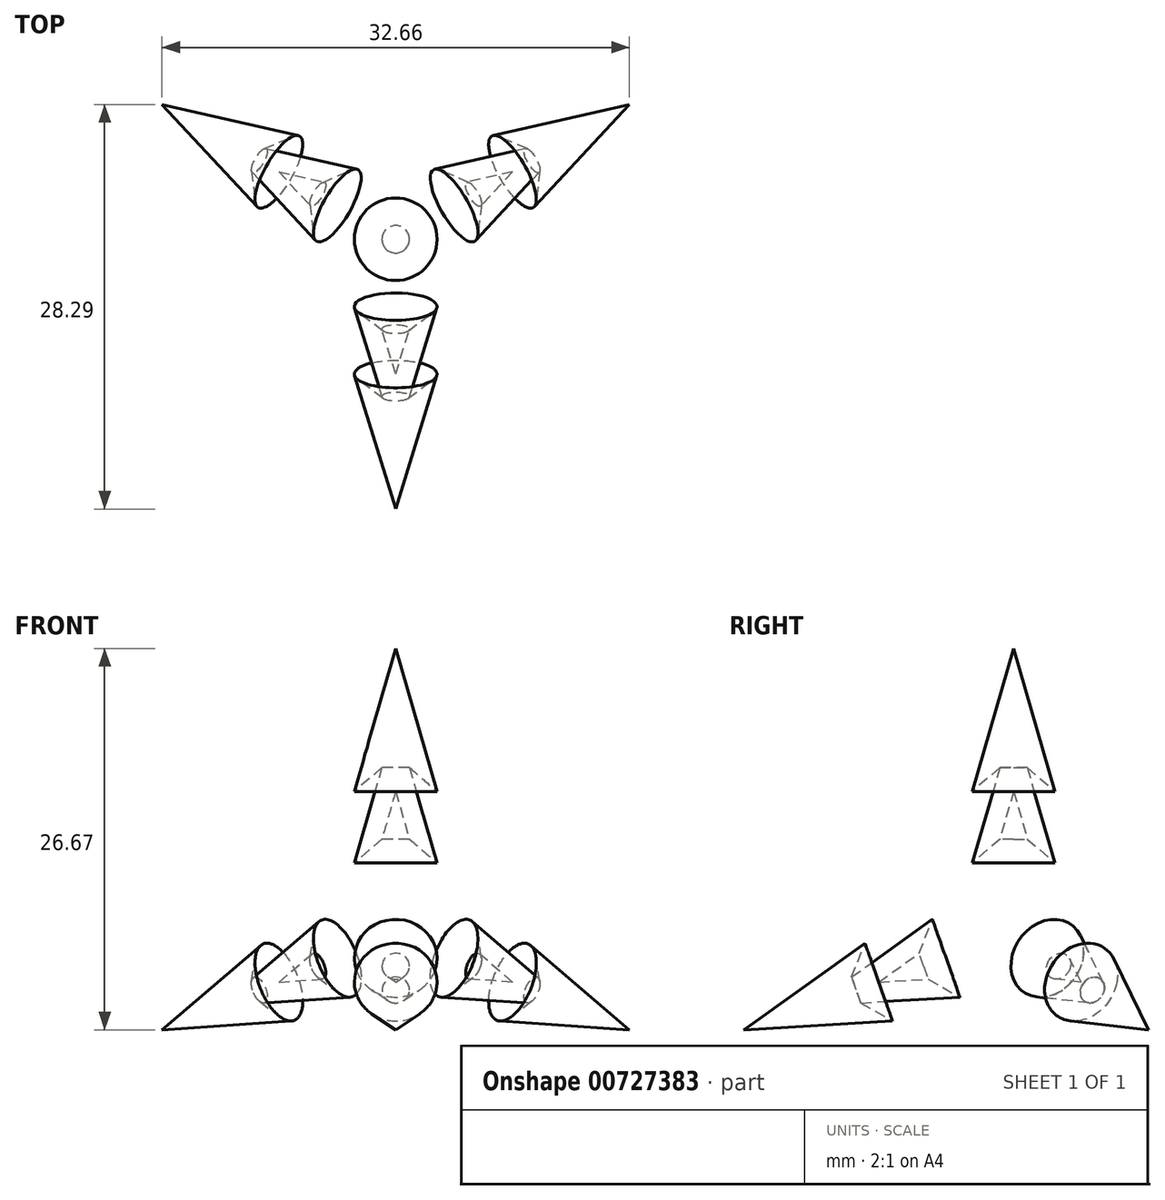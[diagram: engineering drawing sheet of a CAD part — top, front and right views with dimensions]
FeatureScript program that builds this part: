
annotation { "Feature Type Name" : "Feature", "Feature Type Description" : "" }
export const myFeature = defineFeature(function(context is Context, id is Id, definition is map)
    precondition{}
    {
        {
            var Q0;
            Q0=qCreatedBy(makeId("Front.planeOp"),FACE);
            var sketch = newSketch(context, id + "F0", { "sketchPlane" : qUnion([Q0])});
            skCircle(sketch, "E0", {"center": v(0, 0) * mm, "radius": 25 * mm});
            skCircle(sketch, "E1.cCircle", {"center": v(0, 0) * mm, "radius": 25 * mm, "construction": true});
            skLineSegment(sketch, "E2.0", {"start": v(0, 25) * mm, "end": v(21.65, -12.5) * mm});
            skLineSegment(sketch, "E2.1", {"start": v(21.65, -12.5) * mm, "end": v(-21.65, -12.5) * mm});
            skLineSegment(sketch, "E2.2", {"start": v(-21.65, -12.5) * mm, "end": v(0, 25) * mm, "construction": true});
            skLineSegment(sketch, "E3", {"start": v(0, 0) * mm, "end": v(0, 25) * mm});
            skLineSegment(sketch, "E4", {"start": v(0, 0) * mm, "end": v(-14.43, 0) * mm});
            skLineSegment(sketch, "E5", {"start": v(0, 25) * mm, "end": v(0, 20) * mm});
            skLineSegment(sketch, "E6", {"start": v(0, 15) * mm, "end": v(-2.89, 15) * mm, "construction": true});
            skLineSegment(sketch, "E7", {"start": v(-2.89, 15) * mm, "end": v(-2.89, 15) * mm});
            skLineSegment(sketch, "E8", {"start": v(-2.89, 15) * mm, "end": v(0, 25) * mm});
            skLineSegment(sketch, "E9", {"start": v(0, 10) * mm, "end": v(0, 5) * mm});
            skLineSegment(sketch, "E10", {"start": v(0, 0) * mm, "end": v(-2.89, 0) * mm});
            skLineSegment(sketch, "E11", {"start": v(-2.89, 0) * mm, "end": v(0, 10) * mm});
            skLineSegment(sketch, "E12", {"start": v(0, 20) * mm, "end": v(0, 15) * mm});
            skLineSegment(sketch, "E13", {"start": v(0, 10) * mm, "end": v(-2.89, 10) * mm, "construction": true});
            skLineSegment(sketch, "E14", {"start": v(-2.89, 10) * mm, "end": v(0, 20) * mm});
            skPoint(sketch, "E15", {"position": v(0, 5) * mm});
            skLineSegment(sketch, "E16", {"start": v(0, 15) * mm, "end": v(0, 10) * mm});
            skLineSegment(sketch, "E17", {"start": v(0, 5) * mm, "end": v(-2.89, 5) * mm, "construction": true});
            skLineSegment(sketch, "E18", {"start": v(-2.89, 5) * mm, "end": v(0, 15) * mm});
            skLineSegment(sketch, "E19", {"start": v(0, 5) * mm, "end": v(0, 0) * mm});
            skLineSegment(sketch, "E20", {"start": v(0, 17.5) * mm, "end": v(-2.89, 15) * mm});
            skLineSegment(sketch, "E21", {"start": v(0, 12.5) * mm, "end": v(-2.89, 10) * mm});
            skLineSegment(sketch, "E22", {"start": v(0, 7.5) * mm, "end": v(-2.89, 5) * mm});
            skSolve(sketch);
        }
        {
            var Q0;
            Q0=qCreatedBy(makeId("Right.planeOp"),FACE);
            var sketch = newSketch(context, id + "F1", { "sketchPlane" : qUnion([Q0])});
            skCircle(sketch, "E23", {"center": v(0, 0) * mm, "radius": 25 * mm});
            skLineSegment(sketch, "E24", {"start": v(0, 0) * mm, "end": v(0, 25) * mm});
            skCircle(sketch, "E25.cCircle", {"center": v(0, 0) * mm, "radius": 25 * mm, "construction": true});
            skLineSegment(sketch, "E25.0", {"start": v(0, 25) * mm, "end": v(21.65, -12.5) * mm});
            skLineSegment(sketch, "E25.1", {"start": v(21.65, -12.5) * mm, "end": v(-21.65, -12.5) * mm});
            skLineSegment(sketch, "E25.2", {"start": v(-21.65, -12.5) * mm, "end": v(0, 25) * mm});
            skLineSegment(sketch, "E26", {"start": v(0, 0) * mm, "end": v(0, -25) * mm});
            skSolve(sketch);
        }
        {
            var Q0;
            {var subQ0=sQuery(id+"F0.wireOp",EDGE,"E5");Q0=makeQuery(id+"F0.imprint","IMPRINT",FACE,{"disambiguationData":[TD([[makeQuery(id+"F0.imprint","IMPRINT",EDGE,{"derivedFrom":subQ0}),-1.0]])]});}
            var Q1;
            {var subQ0=sQuery(id+"F0.wireOp",EDGE,"E12");var subQ3=sQuery(id+"F0.wireOp",EDGE,"E20");var subQ5=makeQuery(id+"F0.imprint","INTERSECT",VERTEX,{"derivedFrom":[subQ0,subQ3]});Q1=makeQuery(id+"F0.imprint","IMPRINT",FACE,{"disambiguationData":[TD([[makeQuery(id+"F0.imprint","IMPRINT",EDGE,{"disambiguationData":[TD([[subQ5,-1.0]])],"derivedFrom":subQ3}),-1.0]])]});}
            var Q2;
            {var subQ3=sQuery(id+"F0.wireOp",EDGE,"E14");var subQ5=sQuery(id+"F0.wireOp",EDGE,"E21");var subQ6=makeQuery(id+"F0.imprint","INTERSECT",VERTEX,{"derivedFrom":[subQ3,subQ5]});Q2=makeQuery(id+"F0.imprint","IMPRINT",FACE,{"disambiguationData":[TD([[makeQuery(id+"F0.imprint","IMPRINT",EDGE,{"disambiguationData":[TD([[subQ6,-1.0]])],"derivedFrom":subQ3}),-1.0]])]});}
            var Q3;
            {var subQ0=sQuery(id+"F0.wireOp",EDGE,"E16");var subQ3=sQuery(id+"F0.wireOp",EDGE,"E21");var subQ5=makeQuery(id+"F0.imprint","INTERSECT",VERTEX,{"derivedFrom":[subQ0,subQ3]});Q3=makeQuery(id+"F0.imprint","IMPRINT",FACE,{"disambiguationData":[TD([[makeQuery(id+"F0.imprint","IMPRINT",EDGE,{"disambiguationData":[TD([[subQ5,-1.0]])],"derivedFrom":subQ3}),-1.0]])]});}
            var Q4;
            {var subQ3=sQuery(id+"F0.wireOp",EDGE,"E18");var subQ5=sQuery(id+"F0.wireOp",EDGE,"E22");var subQ6=makeQuery(id+"F0.imprint","INTERSECT",VERTEX,{"derivedFrom":[subQ3,subQ5]});Q4=makeQuery(id+"F0.imprint","IMPRINT",FACE,{"disambiguationData":[TD([[makeQuery(id+"F0.imprint","IMPRINT",EDGE,{"disambiguationData":[TD([[subQ6,-1.0]])],"derivedFrom":subQ3}),-1.0]])]});}
            var Q5;
            {var subQ5=sQuery(id+"F0.wireOp",EDGE,"E10");Q5=makeQuery(id+"F0.imprint","IMPRINT",FACE,{"disambiguationData":[TD([[makeQuery(id+"F0.imprint","IMPRINT",EDGE,{"derivedFrom":subQ5}),-1.0]])]});}
            var Q6;
            Q6=sQuery(id+"F0.wireOp",EDGE,"E5");
            revolve(context, id + "F2", {"surfaceOperationType" : NewSurfaceOperationType.NEW, "entities" : qUnion([Q0, Q1, Q2, Q3, Q4, Q5]), "axis" : qUnion([Q6]), "revolveType" : RevolveType.FULL});
        }
        {
            var Q0;
            Q0=qCreatedBy(makeId("Top.planeOp"),FACE);
            var sketch = newSketch(context, id + "F3", { "sketchPlane" : qUnion([Q0])});
            skLineSegment(sketch, "E27", {"start": v(-21.46, 0) * mm, "end": v(21.46, 0) * mm});
            skLineSegment(sketch, "E28", {"start": v(0, 21.76) * mm, "end": v(0, -21.46) * mm});
            skSolve(sketch);
        }
        {
            var Q0;
            Q0=makeQuery(id+"F2.opRevolve","SWEPT_BODY",BODY,{"disambiguationData":[OSD([sQuery(id+"F0.wireOp",EDGE,"E5"),sQuery(id+"F0.wireOp",EDGE,"E8"),sQuery(id+"F0.wireOp",EDGE,"E11"),sQuery(id+"F0.wireOp",EDGE,"E14"),sQuery(id+"F0.wireOp",EDGE,"E18"),sQuery(id+"F0.wireOp",EDGE,"E12"),sQuery(id+"F0.wireOp",EDGE,"E16"),sQuery(id+"F0.wireOp",EDGE,"E20"),sQuery(id+"F0.wireOp",EDGE,"E21"),sQuery(id+"F0.wireOp",EDGE,"E22")])]});
            var Q1;
            Q1=makeQuery(id+"F2.opRevolve","SWEPT_BODY",BODY,{"disambiguationData":[OSD([sQuery(id+"F0.wireOp",EDGE,"E10"),sQuery(id+"F0.wireOp",EDGE,"E11"),sQuery(id+"F0.wireOp",EDGE,"E9"),sQuery(id+"F0.wireOp",EDGE,"E19"),sQuery(id+"F0.wireOp",EDGE,"E22")])]});
            var Q2;
            Q2=sQuery(id+"F3.wireOp",EDGE,"E27");
            transform(context, id + "F4", {"entities" : qUnion([Q0, Q1]), "transformType" : TransformType.ROTATION, "transformAxis" : qUnion([Q2]), "angle" : 109.47 * degree, "makeCopy" : true});
        }
        {
            var Q0;
            Q0=makeQuery(id+"F4.opPattern","COPY",BODY,{"derivedFrom":makeQuery(id+"F2.opRevolve","SWEPT_BODY",BODY,{"disambiguationData":[OSD([sQuery(id+"F0.wireOp",EDGE,"E5"),sQuery(id+"F0.wireOp",EDGE,"E6"),sQuery(id+"F0.wireOp",EDGE,"E8"),sQuery(id+"F0.wireOp",EDGE,"E9"),sQuery(id+"F0.wireOp",EDGE,"E10"),sQuery(id+"F0.wireOp",EDGE,"E11"),sQuery(id+"F0.wireOp",EDGE,"E12"),sQuery(id+"F0.wireOp",EDGE,"E13"),sQuery(id+"F0.wireOp",EDGE,"E14"),sQuery(id+"F0.wireOp",EDGE,"E16"),sQuery(id+"F0.wireOp",EDGE,"E17"),sQuery(id+"F0.wireOp",EDGE,"E18")])]}),"instanceName":"1"});
            var Q1;
            Q1=makeQuery(id+"F4.opPattern","COPY",BODY,{"derivedFrom":makeQuery(id+"F2.opRevolve","SWEPT_BODY",BODY,{"disambiguationData":[OSD([sQuery(id+"F0.wireOp",EDGE,"E10"),sQuery(id+"F0.wireOp",EDGE,"E11"),sQuery(id+"F0.wireOp",EDGE,"E9"),sQuery(id+"F0.wireOp",EDGE,"E19"),sQuery(id+"F0.wireOp",EDGE,"E22")])]}),"instanceName":"1"});
            var Q2;
            Q2=sQuery(id+"F1.wireOp",EDGE,"E26");
            circularPattern(context, id + "F5", {"entities" : qUnion([Q0, Q1]), "axis" : qUnion([Q2]), "angle" : 360 * degree, "instanceCount" : 3, "equalSpace" : true});
        }
    });
